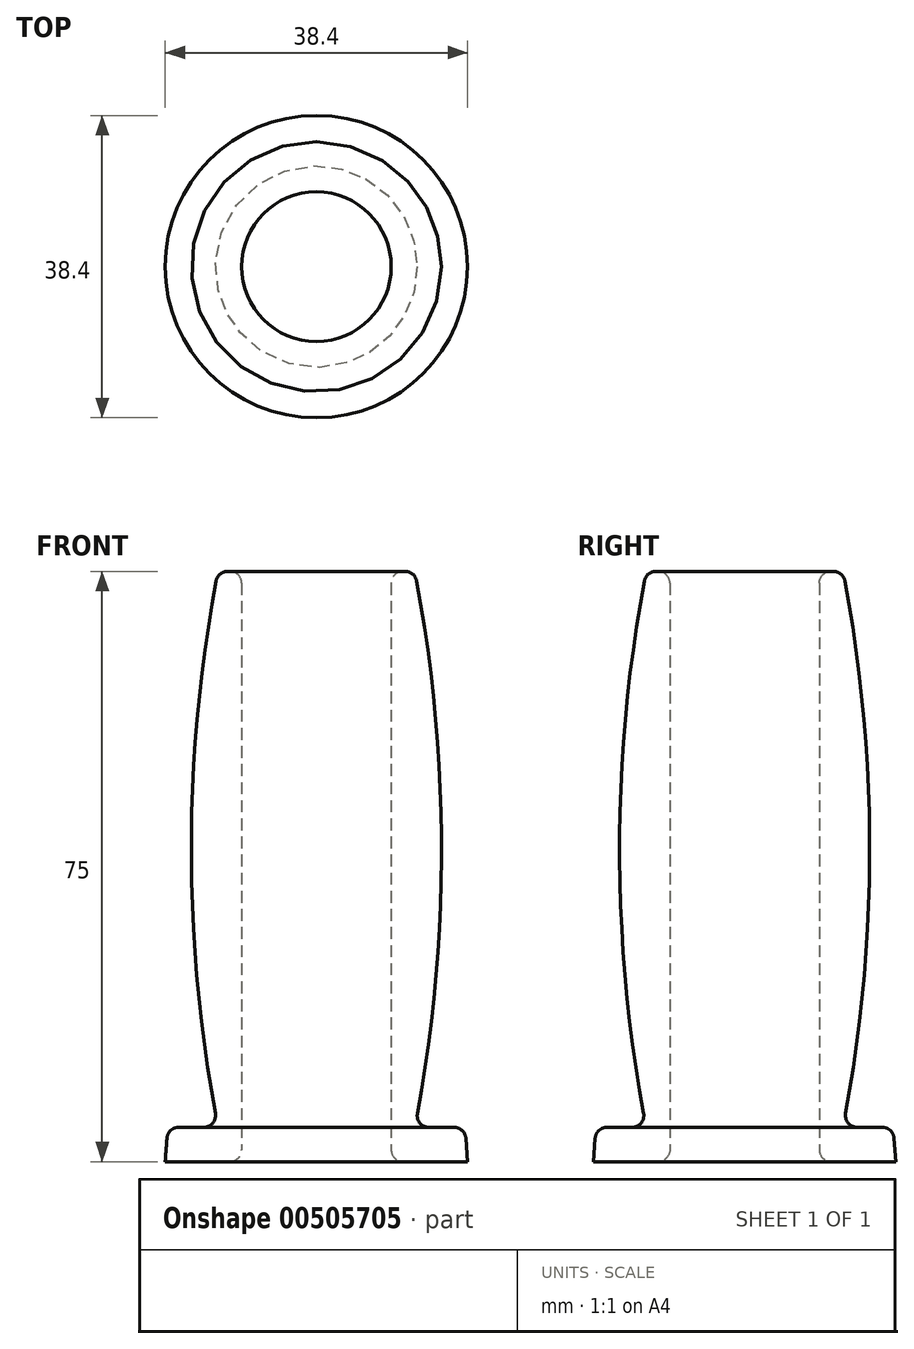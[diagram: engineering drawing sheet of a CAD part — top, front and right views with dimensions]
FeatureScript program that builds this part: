
annotation { "Feature Type Name" : "Feature", "Feature Type Description" : "" }
export const myFeature = defineFeature(function(context is Context, id is Id, definition is map)
    precondition{}
    {
        {
            var Q0;
            Q0=qCreatedBy(makeId("Right.planeOp"),FACE);
            var sketch = newSketch(context, id + "F0", { "sketchPlane" : qUnion([Q0])});
            skLineSegment(sketch, "E0", {"start": v(-9.5, 0) * mm, "end": v(-9.5, 75) * mm});
            skArc(sketch, "E1", {"start": v(-12.5, 75) * mm, "mid": v(-15.89, 39.68) * mm, "end": v(-12.5, 4.35) * mm});
            skLineSegment(sketch, "E2", {"start": v(-12.5, 75) * mm, "end": v(-9.5, 75) * mm});
            skLineSegment(sketch, "E3", {"start": v(-9.5, 0) * mm, "end": v(-19.2, 0) * mm});
            skLineSegment(sketch, "E4", {"start": v(-19.2, 0) * mm, "end": v(-18.89, 4.35) * mm});
            skLineSegment(sketch, "E5", {"start": v(-18.89, 4.35) * mm, "end": v(-12.5, 4.35) * mm});
            skPoint(sketch, "E6.orphan", {"position": v(-9.5, 4.35) * mm});
            skLineSegment(sketch, "E7", {"start": v(0, 0) * mm, "end": v(0, 75.54) * mm, "construction": true});
            skSolve(sketch);
        }
        {
            var Q0;
            Q0=makeQuery(id+"F0.imprint","IMPRINT",FACE,{"disambiguationData":[TD([[makeQuery(id+"F0.imprint","IMPRINT",EDGE,{"derivedFrom":sQuery(id+"F0.wireOp",EDGE,"E0")}),1.0]])]});
            var Q1;
            Q1=sQuery(id+"F0.wireOp",EDGE,"E7");
            revolve(context, id + "F1", {"entities" : qUnion([Q0]), "axis" : qUnion([Q1]), "revolveType" : RevolveType.FULL});
        }
        {
            var Q0;
            Q0=makeQuery(id+"F1.opRevolve","SWEPT_EDGE",EDGE,{"disambiguationData":[OSD([sQuery(id+"F0.wireOp",EDGE,"E0"),sQuery(id+"F0.wireOp",EDGE,"E2")])]});
            var Q1;
            Q1=makeQuery(id+"F1.opRevolve","SWEPT_EDGE",EDGE,{"disambiguationData":[OSD([sQuery(id+"F0.wireOp",EDGE,"E4"),sQuery(id+"F0.wireOp",EDGE,"E5")])]});
            var Q2;
            Q2=makeQuery(id+"F1.opRevolve","SWEPT_EDGE",EDGE,{"disambiguationData":[OSD([sQuery(id+"F0.wireOp",EDGE,"E1"),sQuery(id+"F0.wireOp",EDGE,"E5")])]});
            var Q3;
            Q3=makeQuery(id+"F1.opRevolve","SWEPT_EDGE",EDGE,{"disambiguationData":[OSD([sQuery(id+"F0.wireOp",EDGE,"E1"),sQuery(id+"F0.wireOp",EDGE,"E2")])]});
            var Q4;
            Q4=makeQuery(id+"F1.opRevolve","SWEPT_EDGE",EDGE,{"disambiguationData":[OSD([sQuery(id+"F0.wireOp",EDGE,"E0"),sQuery(id+"F0.wireOp",EDGE,"E3")])]});
            fillet(context, id + "F2", {"entities" : qUnion([Q0, Q1, Q2, Q3, Q4]), "radius" : 1.5 * mm, "tangentPropagation" : true, "allowEdgeOverflow" : false});
        }
    });
